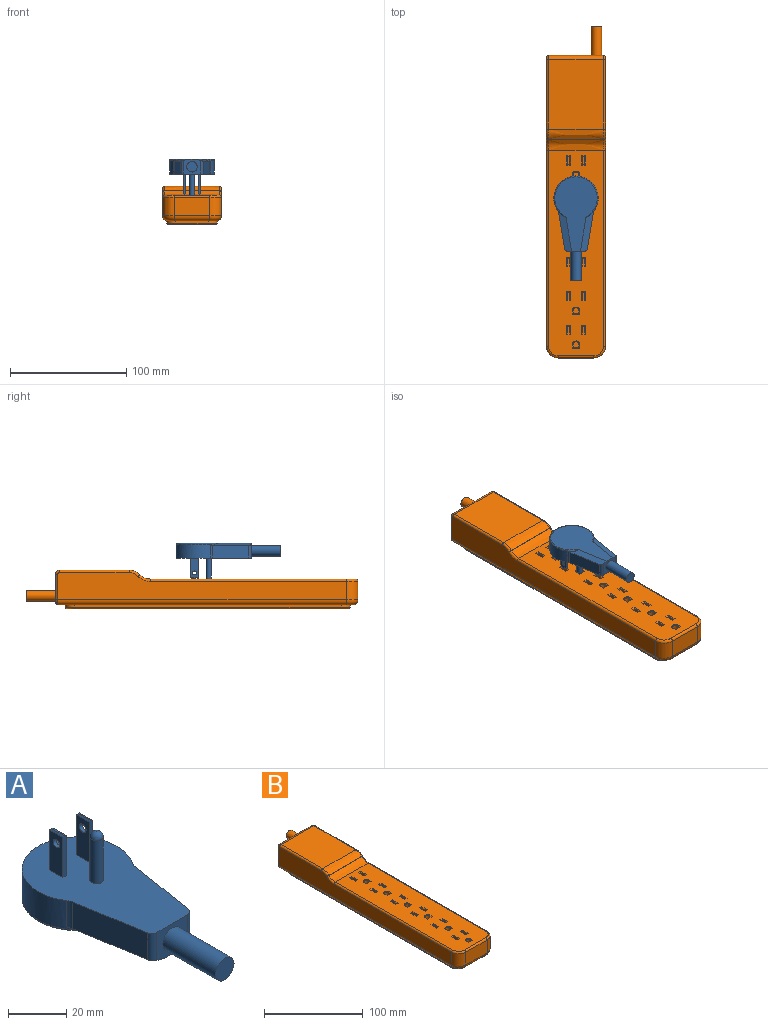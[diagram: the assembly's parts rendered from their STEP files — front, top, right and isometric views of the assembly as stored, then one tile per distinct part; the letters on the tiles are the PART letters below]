
ASSEMBLY  parts=2 mates=1
PART A: 35 faces, bbox 41.3x91.8x33.1 mm
  f0: cylinder r=2.29mm len=18.03mm, axis (0,0,-1), area 259mm2, adj f15,f18
  f1: plane 35.19x12.14mm, normal (-0.26,-0.04,-0.97), area 184.7mm2, adj f11,f12,f14,f19,f30,f32,f33
  f2: plane 16.76x6.35mm, normal (-1,0,0), area 97.9mm2, adj f3,f5,f7,f9,f15
  f3: plane 17.27x1.52mm, normal (0,-1,0), area 26.1mm2, adj f2,f4,f6,f8,f9,f15
  f4: plane 16.76x6.35mm, normal (1,0,0), area 97.9mm2, adj f3,f5,f7,f8,f15
  f5: plane 16.76x1.52mm, normal (0,1,0), area 25.5mm2, adj f2,f4,f10,f15
  f6: plane 5.84x0.51mm, normal (0,0,1), area 3mm2, adj f3,f8,f9,f10
  f7: cylinder r=1.65mm len=3.3mm, axis (1,0,0), area 15.8mm2, adj f2,f4
  f8: plane 6.35x0.51mm, normal (0.71,0,0.71), area 4.4mm2, adj f3,f4,f6,f10
  f9: plane 6.35x0.51mm, normal (-0.71,0,0.71), area 4.4mm2, adj f2,f3,f6,f10
  f10: plane 1.52x0.51mm, normal (0,0.71,0.71), area 0.7mm2, adj f5,f6,f8,f9
  f11: plane 31.02x11.18mm, normal (-0.99,-0.16,0), area 351.5mm2, adj f1,f15,f30,f33
  f12: plane 14.75x12.7mm, normal (0,-1,0), area 120mm2, adj f1,f15,f16,f19,f20,f33,f34
  f13: plane 31.02x11.18mm, normal (0.99,-0.16,0), area 351.5mm2, adj f15,f20,f31,f34
  f14: cylinder r=19.05mm len=38.1mm, axis (0,0,-1), area 988.2mm2, adj f1,f15,f20,f30,f31,f32
  f15: plane 64.77x38.1mm, normal (0,0,1), area 1789.5mm2, adj f0,f2,f3,f4,f5,f11,f12,f13
  f16: cylinder r=4.51mm len=25.4mm, axis (0,1,0), area 719.5mm2, adj f12,f17
  f17: plane 9.02x9.02mm, normal (0,-1,0), area 63.9mm2, adj f16
  f18: sphere r=2.29mm, area 32.8mm2, adj f0
  f19: plane 64.01x36.58mm, normal (0,0,-1), area 1394mm2, adj f1,f12,f20,f32
  f20: plane 35.19x12.14mm, normal (0.26,-0.04,-0.97), area 184.7mm2, adj f12,f13,f14,f19,f31,f32,f34
  f21: plane 16.76x6.35mm, normal (1,0,0), area 97.9mm2, adj f15,f22,f24,f26,f28
  f22: plane 17.27x1.52mm, normal (0,-1,0), area 26.1mm2, adj f15,f21,f23,f25,f27,f28
  f23: plane 16.76x6.35mm, normal (-1,0,0), area 97.9mm2, adj f15,f22,f24,f26,f27
  f24: plane 16.76x1.52mm, normal (0,1,0), area 25.5mm2, adj f15,f21,f23,f29
  f25: plane 5.84x0.51mm, normal (0,0,1), area 3mm2, adj f22,f27,f28,f29
  f26: cylinder r=1.65mm len=3.3mm, axis (-1,0,0), area 15.8mm2, adj f21,f23
  f27: plane 6.35x0.51mm, normal (-0.71,0,0.71), area 4.4mm2, adj f22,f23,f25,f29
  f28: plane 6.35x0.51mm, normal (0.71,0,0.71), area 4.4mm2, adj f21,f22,f25,f29
  f29: plane 1.52x0.51mm, normal (0,0.71,0.71), area 0.7mm2, adj f24,f25,f27,f28
  f30: cylinder r=5.08mm len=11.18mm, axis (0,0,-1), area 24mm2, adj f1,f11,f14,f15
  f31: cylinder r=5.08mm len=11.18mm, axis (0,0,-1), area 24mm2, adj f13,f14,f15,f20
  f32: torus R=18.29mm, axis (0,0,1), area 116.6mm2, adj f1,f14,f19,f20
  f33: cylinder r=2.54mm len=11.74mm, axis (0,0,-1), area 40.6mm2, adj f1,f11,f12,f15
  f34: cylinder r=2.54mm len=11.74mm, axis (0,0,1), area 40.6mm2, adj f12,f13,f15,f20
PART B: 224 faces, bbox 55.9x286.6x33 mm
  f0: plane 42.16x7.42mm, normal (0,0,-1), area 110.4mm2, adj f124,f187,f188,f189,f190,f191,f213,f214
  f1: plane 176.98x46.99mm, normal (0,0,1), area 7749.2mm2, adj f8,f26,f27,f28,f29,f30,f31,f32
  f2: plane 59.76x46.99mm, normal (0,0,1), area 2808.3mm2, adj f7,f113,f199,f200
  f3: plane 30.48x15.88mm, normal (0,-1,0), area 483.9mm2, adj f9,f10,f191,f211
  f4: plane 248.29x23.5mm, normal (1,0,0), area 4474.1mm2, adj f10,f187,f195,f197,f199,f201,f203,f205
  f5: plane 248.29x23.5mm, normal (-1,0,0), area 4474.1mm2, adj f9,f188,f196,f198,f200,f202,f204,f206
  f6: plane 46.99x0.18mm, normal (0,-0.71,0.71), area 12mm2, adj f7,f8,f203,f204
  f7: bspline ~55.88x8.98mm, area 469.5mm2, adj f2,f6,f201,f202
  f8: bspline ~55.88x8.98mm, area 469.5mm2, adj f1,f6,f205,f206
  f9: cylinder r=10.16mm len=15.88mm, axis (0,0,-1), area 253.4mm2, adj f3,f5,f190,f210
  f10: cylinder r=10.16mm len=15.88mm, axis (0,0,1), area 253.4mm2, adj f3,f4,f189,f209
  f11: cylinder r=2.54mm len=21.21mm, axis (0,0,1), area 169.2mm2, adj f12,f14,f15,f28
  f12: plane 21.21x2.54mm, normal (1,0,0), area 53.9mm2, adj f11,f13,f15,f29
  f13: plane 21.21x5.08mm, normal (0,1,0), area 107.7mm2, adj f12,f14,f15,f27
  f14: plane 21.21x2.54mm, normal (-1,0,0), area 53.9mm2, adj f11,f13,f15,f26
  f15: plane 5.08x5.08mm, normal (0,0,1), area 23mm2, adj f11,f12,f13,f14
  f16: plane 21.21x2.03mm, normal (0,1,0), area 43.1mm2, adj f17,f19,f20,f37
  f17: plane 21.21x6.86mm, normal (-1,0,0), area 145.5mm2, adj f16,f18,f20,f36
  f18: plane 21.21x2.03mm, normal (0,-1,0), area 43.1mm2, adj f17,f19,f20,f34
  f19: plane 21.21x6.86mm, normal (1,0,0), area 145.5mm2, adj f16,f18,f20,f35
  f20: plane 6.86x2.03mm, normal (0,0,1), area 13.9mm2, adj f16,f17,f18,f19
  f21: plane 21.21x2.03mm, normal (0,1,0), area 43.1mm2, adj f22,f24,f25,f33
  f22: plane 21.21x6.86mm, normal (-1,0,0), area 145.5mm2, adj f21,f23,f25,f31
  f23: plane 21.21x2.03mm, normal (0,-1,0), area 43.1mm2, adj f22,f24,f25,f30
  f24: plane 21.21x6.86mm, normal (1,0,0), area 145.5mm2, adj f21,f23,f25,f32
  f25: plane 6.86x2.03mm, normal (0,0,1), area 13.9mm2, adj f21,f22,f23,f24
  f26: plane 3.18x0.64mm, normal (-0.71,0,0.71), area 2.6mm2, adj f1,f14,f27,f28
  f27: plane 6.35x0.64mm, normal (0,0.71,0.71), area 5.1mm2, adj f1,f13,f26,f29
  f28: cone r=3.17mm half-angle=45deg, axis (0,0,1), area 8.1mm2, adj f1,f11,f26,f29
  f29: plane 3.18x0.64mm, normal (0.71,0,0.71), area 2.6mm2, adj f1,f12,f27,f28
  f30: plane 3.3x0.64mm, normal (0,-0.71,0.71), area 2.4mm2, adj f1,f23,f31,f32
  f31: plane 8.13x0.64mm, normal (-0.71,0,0.71), area 6.7mm2, adj f1,f22,f30,f33
  f32: plane 8.13x0.64mm, normal (0.71,0,0.71), area 6.7mm2, adj f1,f24,f30,f33
  f33: plane 3.3x0.64mm, normal (0,0.71,0.71), area 2.4mm2, adj f1,f21,f31,f32
  f34: plane 3.3x0.64mm, normal (0,-0.71,0.71), area 2.4mm2, adj f1,f18,f35,f36
  f35: plane 8.13x0.64mm, normal (0.71,0,0.71), area 6.7mm2, adj f1,f19,f34,f37
  f36: plane 8.13x0.64mm, normal (-0.71,0,0.71), area 6.7mm2, adj f1,f17,f34,f37
  f37: plane 3.3x0.64mm, normal (0,0.71,0.71), area 2.4mm2, adj f1,f16,f35,f36
  f38: plane 21.21x6.86mm, normal (1,0,0), area 145.5mm2, adj f39,f41,f42,f128
  f39: plane 21.21x2.03mm, normal (0,1,0), area 43.1mm2, adj f38,f40,f42,f130
  f40: plane 21.21x6.86mm, normal (-1,0,0), area 145.5mm2, adj f39,f41,f42,f129
  f41: plane 21.21x2.03mm, normal (0,-1,0), area 43.1mm2, adj f38,f40,f42,f127
  f42: plane 6.86x2.03mm, normal (0,0,1), area 13.9mm2, adj f38,f39,f40,f41
  f43: plane 21.21x6.86mm, normal (1,0,0), area 145.5mm2, adj f44,f46,f47,f133
  f44: plane 21.21x2.03mm, normal (0,1,0), area 43.1mm2, adj f43,f45,f47,f131
  f45: plane 21.21x6.86mm, normal (-1,0,0), area 145.5mm2, adj f44,f46,f47,f132
  f46: plane 21.21x2.03mm, normal (0,-1,0), area 43.1mm2, adj f43,f45,f47,f134
  f47: plane 6.86x2.03mm, normal (0,0,1), area 13.9mm2, adj f43,f44,f45,f46
  f48: plane 21.21x2.54mm, normal (1,0,0), area 53.9mm2, adj f49,f51,f52,f136
  f49: plane 21.21x5.08mm, normal (0,1,0), area 107.7mm2, adj f48,f50,f52,f138
  f50: plane 21.21x2.54mm, normal (-1,0,0), area 53.9mm2, adj f49,f51,f52,f137
  f51: cylinder r=2.54mm len=21.21mm, axis (0,0,1), area 169.2mm2, adj f48,f50,f52,f135
  f52: plane 5.08x5.08mm, normal (0,0,1), area 23mm2, adj f48,f49,f50,f51
  f53: plane 21.21x6.86mm, normal (1,0,0), area 145.5mm2, adj f54,f56,f57,f144
  f54: plane 21.21x2.03mm, normal (0,1,0), area 43.1mm2, adj f53,f55,f57,f146
  f55: plane 21.21x6.86mm, normal (-1,0,0), area 145.5mm2, adj f54,f56,f57,f145
  f56: plane 21.21x2.03mm, normal (0,-1,0), area 43.1mm2, adj f53,f55,f57,f143
  f57: plane 6.86x2.03mm, normal (0,0,1), area 13.9mm2, adj f53,f54,f55,f56
  f58: plane 21.21x6.86mm, normal (1,0,0), area 145.5mm2, adj f59,f61,f62,f140
  f59: plane 21.21x2.03mm, normal (0,1,0), area 43.1mm2, adj f58,f60,f62,f139
  f60: plane 21.21x6.86mm, normal (-1,0,0), area 145.5mm2, adj f59,f61,f62,f141
  f61: plane 21.21x2.03mm, normal (0,-1,0), area 43.1mm2, adj f58,f60,f62,f142
  f62: plane 6.86x2.03mm, normal (0,0,1), area 13.9mm2, adj f58,f59,f60,f61
  f63: plane 21.21x2.54mm, normal (1,0,0), area 53.9mm2, adj f64,f66,f67,f151
  f64: plane 21.21x5.08mm, normal (0,1,0), area 107.7mm2, adj f63,f65,f67,f152
  f65: plane 21.21x2.54mm, normal (-1,0,0), area 53.9mm2, adj f64,f66,f67,f154
  f66: cylinder r=2.54mm len=21.21mm, axis (0,0,1), area 169.2mm2, adj f63,f65,f67,f153
  f67: plane 5.08x5.08mm, normal (0,0,1), area 23mm2, adj f63,f64,f65,f66
  f68: plane 21.21x6.86mm, normal (1,0,0), area 145.5mm2, adj f69,f71,f72,f160
  f69: plane 21.21x2.03mm, normal (0,1,0), area 43.1mm2, adj f68,f70,f72,f162
  f70: plane 21.21x6.86mm, normal (-1,0,0), area 145.5mm2, adj f69,f71,f72,f161
  f71: plane 21.21x2.03mm, normal (0,-1,0), area 43.1mm2, adj f68,f70,f72,f159
  f72: plane 6.86x2.03mm, normal (0,0,1), area 13.9mm2, adj f68,f69,f70,f71
  f73: plane 21.21x6.86mm, normal (1,0,0), area 145.5mm2, adj f74,f76,f77,f156
  f74: plane 21.21x2.03mm, normal (0,1,0), area 43.1mm2, adj f73,f75,f77,f155
  f75: plane 21.21x6.86mm, normal (-1,0,0), area 145.5mm2, adj f74,f76,f77,f157
  f76: plane 21.21x2.03mm, normal (0,-1,0), area 43.1mm2, adj f73,f75,f77,f158
  f77: plane 6.86x2.03mm, normal (0,0,1), area 13.9mm2, adj f73,f74,f75,f76
  f78: plane 21.21x2.54mm, normal (1,0,0), area 53.9mm2, adj f79,f81,f82,f150
  f79: plane 21.21x5.08mm, normal (0,1,0), area 107.7mm2, adj f78,f80,f82,f148
  f80: plane 21.21x2.54mm, normal (-1,0,0), area 53.9mm2, adj f79,f81,f82,f147
  f81: cylinder r=2.54mm len=21.21mm, axis (0,0,1), area 169.2mm2, adj f78,f80,f82,f149
  f82: plane 5.08x5.08mm, normal (0,0,1), area 23mm2, adj f78,f79,f80,f81
  f83: plane 21.21x2.54mm, normal (1,0,0), area 53.9mm2, adj f84,f86,f87,f186
  f84: plane 21.21x5.08mm, normal (0,1,0), area 107.7mm2, adj f83,f85,f87,f184
  f85: plane 21.21x2.54mm, normal (-1,0,0), area 53.9mm2, adj f84,f86,f87,f183
  f86: cylinder r=2.54mm len=21.21mm, axis (0,0,1), area 169.2mm2, adj f83,f85,f87,f185
  f87: plane 5.08x5.08mm, normal (0,0,1), area 23mm2, adj f83,f84,f85,f86
  f88: plane 21.21x6.86mm, normal (1,0,0), area 145.5mm2, adj f89,f91,f92,f168
  f89: plane 21.21x2.03mm, normal (0,1,0), area 43.1mm2, adj f88,f90,f92,f170
  f90: plane 21.21x6.86mm, normal (-1,0,0), area 145.5mm2, adj f89,f91,f92,f169
  f91: plane 21.21x2.03mm, normal (0,-1,0), area 43.1mm2, adj f88,f90,f92,f167
  f92: plane 6.86x2.03mm, normal (0,0,1), area 13.9mm2, adj f88,f89,f90,f91
  f93: plane 21.21x6.86mm, normal (1,0,0), area 145.5mm2, adj f94,f96,f97,f172
  f94: plane 21.21x2.03mm, normal (0,1,0), area 43.1mm2, adj f93,f95,f97,f174
  f95: plane 21.21x6.86mm, normal (-1,0,0), area 145.5mm2, adj f94,f96,f97,f173
  f96: plane 21.21x2.03mm, normal (0,-1,0), area 43.1mm2, adj f93,f95,f97,f171
  f97: plane 6.86x2.03mm, normal (0,0,1), area 13.9mm2, adj f93,f94,f95,f96
  f98: plane 21.21x2.54mm, normal (1,0,0), area 53.9mm2, adj f99,f101,f102,f163
  f99: plane 21.21x5.08mm, normal (0,1,0), area 107.7mm2, adj f98,f100,f102,f164
  f100: plane 21.21x2.54mm, normal (-1,0,0), area 53.9mm2, adj f99,f101,f102,f166
  f101: cylinder r=2.54mm len=21.21mm, axis (0,0,1), area 169.2mm2, adj f98,f100,f102,f165
  f102: plane 5.08x5.08mm, normal (0,0,1), area 23mm2, adj f98,f99,f100,f101
  f103: plane 21.21x6.86mm, normal (1,0,0), area 145.5mm2, adj f104,f106,f107,f180
  f104: plane 21.21x2.03mm, normal (0,1,0), area 43.1mm2, adj f103,f105,f107,f182
  f105: plane 21.21x6.86mm, normal (-1,0,0), area 145.5mm2, adj f104,f106,f107,f181
  f106: plane 21.21x2.03mm, normal (0,-1,0), area 43.1mm2, adj f103,f105,f107,f179
  f107: plane 6.86x2.03mm, normal (0,0,1), area 13.9mm2, adj f103,f104,f105,f106
  f108: plane 21.21x6.86mm, normal (1,0,0), area 145.5mm2, adj f109,f111,f112,f177
  f109: plane 21.21x2.03mm, normal (0,1,0), area 43.1mm2, adj f108,f110,f112,f175
  f110: plane 21.21x6.86mm, normal (-1,0,0), area 145.5mm2, adj f109,f111,f112,f176
  f111: plane 21.21x2.03mm, normal (0,-1,0), area 43.1mm2, adj f108,f110,f112,f178
  f112: plane 6.86x2.03mm, normal (0,0,1), area 13.9mm2, adj f108,f109,f110,f111
  f113: cylinder r=3.56mm len=46.99mm, axis (-1,0,0), area 262.5mm2, adj f2,f118,f197,f198
  f114: plane 24.64x3.55mm, normal (-1,0,0), area 87.1mm2, adj f115,f118,f119,f193,f195
  f115: plane 47.24x3.52mm, normal (0,0,1), area 165.5mm2, adj f114,f116,f119,f192,f193,f194
  f116: plane 24.64x3.55mm, normal (1,0,0), area 87.1mm2, adj f115,f118,f119,f194,f196
  f117: cylinder r=4.51mm len=28.96mm, axis (0,1,0), area 820.3mm2, adj f119,f120
  f118: plane 47.24x3.56mm, normal (0,0,-1), area 168mm2, adj f113,f114,f116,f119,f197,f198
  f119: plane 47.24x24.64mm, normal (0,1,0), area 1100.1mm2, adj f114,f115,f116,f117,f118
  f120: plane 9.02x9.02mm, normal (0,1,0), area 63.9mm2, adj f117
  f121: plane 42.16x11.51mm, normal (0,0,-1), area 297.2mm2, adj f122,f187,f188,f192,f212,f215
  f122: plane 28.18x2.03mm, normal (0,1,0), area 57.3mm2, adj f121,f212,f215,f221
  f123: plane 229.72x2.06mm, normal (1,0,0), area 473.7mm2, adj f187,f212,f213,f222
  f124: plane 28.18x2.03mm, normal (0,-1,0), area 57.3mm2, adj f0,f213,f214,f218
  f125: plane 229.72x2.1mm, normal (-1,0,0), area 481.6mm2, adj f188,f214,f215,f217
  f126: plane 242.42x40.88mm, normal (0,0,-1), area 9874.8mm2, adj f216,f217,f218,f219,f220,f221,f222,f223
  f127: plane 3.3x0.64mm, normal (0,-0.71,0.71), area 2.4mm2, adj f1,f41,f128,f129
  f128: plane 8.13x0.64mm, normal (0.71,0,0.71), area 6.7mm2, adj f1,f38,f127,f130
  f129: plane 8.13x0.64mm, normal (-0.71,0,0.71), area 6.7mm2, adj f1,f40,f127,f130
  f130: plane 3.3x0.64mm, normal (0,0.71,0.71), area 2.4mm2, adj f1,f39,f128,f129
  f131: plane 3.3x0.64mm, normal (0,0.71,0.71), area 2.4mm2, adj f1,f44,f132,f133
  f132: plane 8.13x0.64mm, normal (-0.71,0,0.71), area 6.7mm2, adj f1,f45,f131,f134
  f133: plane 8.13x0.64mm, normal (0.71,0,0.71), area 6.7mm2, adj f1,f43,f131,f134
  f134: plane 3.3x0.64mm, normal (0,-0.71,0.71), area 2.4mm2, adj f1,f46,f132,f133
  f135: cone r=3.17mm half-angle=45deg, axis (0,0,1), area 8.1mm2, adj f1,f51,f136,f137
  f136: plane 3.18x0.64mm, normal (0.71,0,0.71), area 2.6mm2, adj f1,f48,f135,f138
  f137: plane 3.18x0.64mm, normal (-0.71,0,0.71), area 2.6mm2, adj f1,f50,f135,f138
  f138: plane 6.35x0.64mm, normal (0,0.71,0.71), area 5.1mm2, adj f1,f49,f136,f137
  f139: plane 3.3x0.64mm, normal (0,0.71,0.71), area 2.4mm2, adj f1,f59,f140,f141
  f140: plane 8.13x0.64mm, normal (0.71,0,0.71), area 6.7mm2, adj f1,f58,f139,f142
  f141: plane 8.13x0.64mm, normal (-0.71,0,0.71), area 6.7mm2, adj f1,f60,f139,f142
  f142: plane 3.3x0.64mm, normal (0,-0.71,0.71), area 2.4mm2, adj f1,f61,f140,f141
  f143: plane 3.3x0.64mm, normal (0,-0.71,0.71), area 2.4mm2, adj f1,f56,f144,f145
  f144: plane 8.13x0.64mm, normal (0.71,0,0.71), area 6.7mm2, adj f1,f53,f143,f146
  f145: plane 8.13x0.64mm, normal (-0.71,0,0.71), area 6.7mm2, adj f1,f55,f143,f146
  f146: plane 3.3x0.64mm, normal (0,0.71,0.71), area 2.4mm2, adj f1,f54,f144,f145
  f147: plane 3.18x0.64mm, normal (-0.71,0,0.71), area 2.6mm2, adj f1,f80,f148,f149
  f148: plane 6.35x0.64mm, normal (0,0.71,0.71), area 5.1mm2, adj f1,f79,f147,f150
  f149: cone r=3.17mm half-angle=45deg, axis (0,0,1), area 8.1mm2, adj f1,f81,f147,f150
  f150: plane 3.18x0.64mm, normal (0.71,0,0.71), area 2.6mm2, adj f1,f78,f148,f149
  f151: plane 3.18x0.64mm, normal (0.71,0,0.71), area 2.6mm2, adj f1,f63,f152,f153
  f152: plane 6.35x0.64mm, normal (0,0.71,0.71), area 5.1mm2, adj f1,f64,f151,f154
  f153: cone r=3.17mm half-angle=45deg, axis (0,0,1), area 8.1mm2, adj f1,f66,f151,f154
  f154: plane 3.18x0.64mm, normal (-0.71,0,0.71), area 2.6mm2, adj f1,f65,f152,f153
  f155: plane 3.3x0.64mm, normal (0,0.71,0.71), area 2.4mm2, adj f1,f74,f156,f157
  f156: plane 8.13x0.64mm, normal (0.71,0,0.71), area 6.7mm2, adj f1,f73,f155,f158
  f157: plane 8.13x0.64mm, normal (-0.71,0,0.71), area 6.7mm2, adj f1,f75,f155,f158
  f158: plane 3.3x0.64mm, normal (0,-0.71,0.71), area 2.4mm2, adj f1,f76,f156,f157
  f159: plane 3.3x0.64mm, normal (0,-0.71,0.71), area 2.4mm2, adj f1,f71,f160,f161
  f160: plane 8.13x0.64mm, normal (0.71,0,0.71), area 6.7mm2, adj f1,f68,f159,f162
  f161: plane 8.13x0.64mm, normal (-0.71,0,0.71), area 6.7mm2, adj f1,f70,f159,f162
  f162: plane 3.3x0.64mm, normal (0,0.71,0.71), area 2.4mm2, adj f1,f69,f160,f161
  f163: plane 3.18x0.64mm, normal (0.71,0,0.71), area 2.6mm2, adj f1,f98,f164,f165
  f164: plane 6.35x0.64mm, normal (0,0.71,0.71), area 5.1mm2, adj f1,f99,f163,f166
  f165: cone r=3.17mm half-angle=45deg, axis (0,0,1), area 8.1mm2, adj f1,f101,f163,f166
  f166: plane 3.18x0.64mm, normal (-0.71,0,0.71), area 2.6mm2, adj f1,f100,f164,f165
  f167: plane 3.3x0.64mm, normal (0,-0.71,0.71), area 2.4mm2, adj f1,f91,f168,f169
  f168: plane 8.13x0.64mm, normal (0.71,0,0.71), area 6.7mm2, adj f1,f88,f167,f170
  f169: plane 8.13x0.64mm, normal (-0.71,0,0.71), area 6.7mm2, adj f1,f90,f167,f170
  f170: plane 3.3x0.64mm, normal (0,0.71,0.71), area 2.4mm2, adj f1,f89,f168,f169
  f171: plane 3.3x0.64mm, normal (0,-0.71,0.71), area 2.4mm2, adj f1,f96,f172,f173
  f172: plane 8.13x0.64mm, normal (0.71,0,0.71), area 6.7mm2, adj f1,f93,f171,f174
  f173: plane 8.13x0.64mm, normal (-0.71,0,0.71), area 6.7mm2, adj f1,f95,f171,f174
  f174: plane 3.3x0.64mm, normal (0,0.71,0.71), area 2.4mm2, adj f1,f94,f172,f173
  f175: plane 3.3x0.64mm, normal (0,0.71,0.71), area 2.4mm2, adj f1,f109,f176,f177
  f176: plane 8.13x0.64mm, normal (-0.71,0,0.71), area 6.7mm2, adj f1,f110,f175,f178
  f177: plane 8.13x0.64mm, normal (0.71,0,0.71), area 6.7mm2, adj f1,f108,f175,f178
  f178: plane 3.3x0.64mm, normal (0,-0.71,0.71), area 2.4mm2, adj f1,f111,f176,f177
  f179: plane 3.3x0.64mm, normal (0,-0.71,0.71), area 2.4mm2, adj f1,f106,f180,f181
  f180: plane 8.13x0.64mm, normal (0.71,0,0.71), area 6.7mm2, adj f1,f103,f179,f182
  f181: plane 8.13x0.64mm, normal (-0.71,0,0.71), area 6.7mm2, adj f1,f105,f179,f182
  f182: plane 3.3x0.64mm, normal (0,0.71,0.71), area 2.4mm2, adj f1,f104,f180,f181
  f183: plane 3.18x0.64mm, normal (-0.71,0,0.71), area 2.6mm2, adj f1,f85,f184,f185
  f184: plane 6.35x0.64mm, normal (0,0.71,0.71), area 5.1mm2, adj f1,f84,f183,f186
  f185: cone r=3.17mm half-angle=45deg, axis (0,0,1), area 8.1mm2, adj f1,f86,f183,f186
  f186: plane 3.18x0.64mm, normal (0.71,0,0.71), area 2.6mm2, adj f1,f83,f184,f185
  f187: cylinder r=4.32mm len=248.29mm, axis (0,-1,0), area 1565.7mm2, adj f0,f4,f121,f123,f189,f193,f212,f213
  f188: cylinder r=4.32mm len=248.29mm, axis (0,1,0), area 1508.9mm2, adj f0,f5,f121,f125,f190,f194,f214,f215
  f189: torus R=5.84mm, axis (0,0,-1), area 91.5mm2, adj f0,f10,f187,f191
  f190: torus R=5.84mm, axis (0,0,-1), area 91.5mm2, adj f0,f9,f188,f191
  f191: cylinder r=4.32mm len=30.48mm, axis (-1,0,0), area 206.7mm2, adj f0,f3,f189,f190
  f192: cylinder r=1.91mm len=42.16mm, axis (1,0,0), area 110mm2, adj f115,f121,f193,f194
  f193: torus R=2.41mm, axis (0,-1,0), area 14.4mm2, adj f114,f115,f187,f192,f195
  f194: torus R=2.41mm, axis (0,-1,0), area 14.4mm2, adj f115,f116,f188,f192,f196
  f195: cylinder r=1.91mm len=21.84mm, axis (0,0,-1), area 62.6mm2, adj f4,f114,f193,f197
  f196: cylinder r=1.91mm len=21.84mm, axis (0,0,1), area 62.6mm2, adj f5,f116,f194,f198
  f197: torus R=1.65mm, axis (1,0,0), area 13.5mm2, adj f4,f113,f118,f195,f199
  f198: torus R=1.65mm, axis (1,0,0), area 13.5mm2, adj f5,f113,f118,f196,f200
  f199: cylinder r=1.91mm len=59.76mm, axis (0,1,0), area 178.8mm2, adj f2,f4,f197,f201
  f200: cylinder r=1.91mm len=59.76mm, axis (0,-1,0), area 178.8mm2, adj f2,f5,f198,f202
  f201: bspline ~12.88x5.65mm, area 28.3mm2, adj f4,f7,f199,f203
  f202: bspline ~12.18x7.38mm, area 28.3mm2, adj f5,f7,f200,f204
  f203: cylinder r=1.91mm len=1.91mm, axis (0,-0.71,-0.71), area 0.8mm2, adj f4,f6,f201,f205
  f204: cylinder r=1.91mm len=1.91mm, axis (0,-0.71,-0.71), area 0.8mm2, adj f5,f6,f202,f206
  f205: bspline ~15.92x7.94mm, area 31.5mm2, adj f4,f8,f203,f207
  f206: bspline ~15.92x7.94mm, area 31.5mm2, adj f5,f8,f204,f208
  f207: cylinder r=1.91mm len=168.73mm, axis (0,1,0), area 504.9mm2, adj f1,f4,f205,f209
  f208: cylinder r=1.91mm len=168.73mm, axis (0,-1,0), area 504.9mm2, adj f1,f5,f206,f210
  f209: torus R=8.26mm, axis (0,0,-1), area 44.5mm2, adj f1,f10,f207,f211
  f210: torus R=8.26mm, axis (0,0,-1), area 44.5mm2, adj f1,f9,f208,f211
  f211: cylinder r=1.91mm len=30.48mm, axis (1,0,0), area 91.2mm2, adj f1,f3,f209,f210
  f212: cylinder r=7.62mm len=7.62mm, axis (0,0,-1), area 24.4mm2, adj f121,f122,f123,f187,f223
  f213: cylinder r=7.62mm len=7.62mm, axis (0,0,1), area 24.4mm2, adj f0,f123,f124,f187,f220
  f214: cylinder r=7.62mm len=7.62mm, axis (0,0,-1), area 24.4mm2, adj f0,f124,f125,f188,f216
  f215: cylinder r=7.62mm len=7.62mm, axis (0,0,1), area 24.4mm2, adj f121,f122,f125,f188,f219
  f216: torus R=6.35mm, axis (0,0,-1), area 22.4mm2, adj f126,f214,f217,f218
  f217: cylinder r=1.27mm len=229.72mm, axis (0,1,0), area 458.3mm2, adj f125,f126,f216,f219
  f218: cylinder r=1.27mm len=28.18mm, axis (-1,0,0), area 56.2mm2, adj f124,f126,f216,f220
  f219: torus R=6.35mm, axis (0,0,-1), area 22.4mm2, adj f126,f215,f217,f221
  f220: torus R=6.35mm, axis (0,0,-1), area 22.4mm2, adj f126,f213,f218,f222
  f221: cylinder r=1.27mm len=28.18mm, axis (1,0,0), area 56.2mm2, adj f122,f126,f219,f223
  f222: cylinder r=1.27mm len=229.72mm, axis (0,-1,0), area 458.3mm2, adj f123,f126,f220,f223
  f223: torus R=6.35mm, axis (0,0,-1), area 22.4mm2, adj f126,f212,f221,f222
PLACE A rot(axis=(0,-1,0),180deg) t=(-42.05,-259.34,80.45)mm
PLACE B t=(-42.05,-136.53,24.32)mm
MATE slider A.f0 <-> B.f1  axis (0,0,-1) through (-42.05,-268.48,49.72)mm
